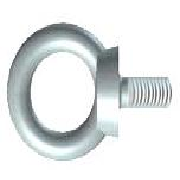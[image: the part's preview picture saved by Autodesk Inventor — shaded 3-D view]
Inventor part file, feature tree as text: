
AUTODESK INVENTOR PART (.ipt)
format: ipt  version: 2024 (Build 280153000, 153)  size: 257,024 bytes
history: native  units: mm (DEFAULTED — no unit token found)
features: extrude x2, other x1
ambient origin geometry x8: Origin, YZ Plane, XZ Plane, XY Plane, X Axis, Y Axis, Z Axis, Center Point
bodies: Solid1 (feature_tree), Body (feature_tree)
feature tree (3):
  extrude  "Eye"  Depth=35.0mm
  extrude  "Cut"  Depth=72.0mm
  other  "Groove1"
